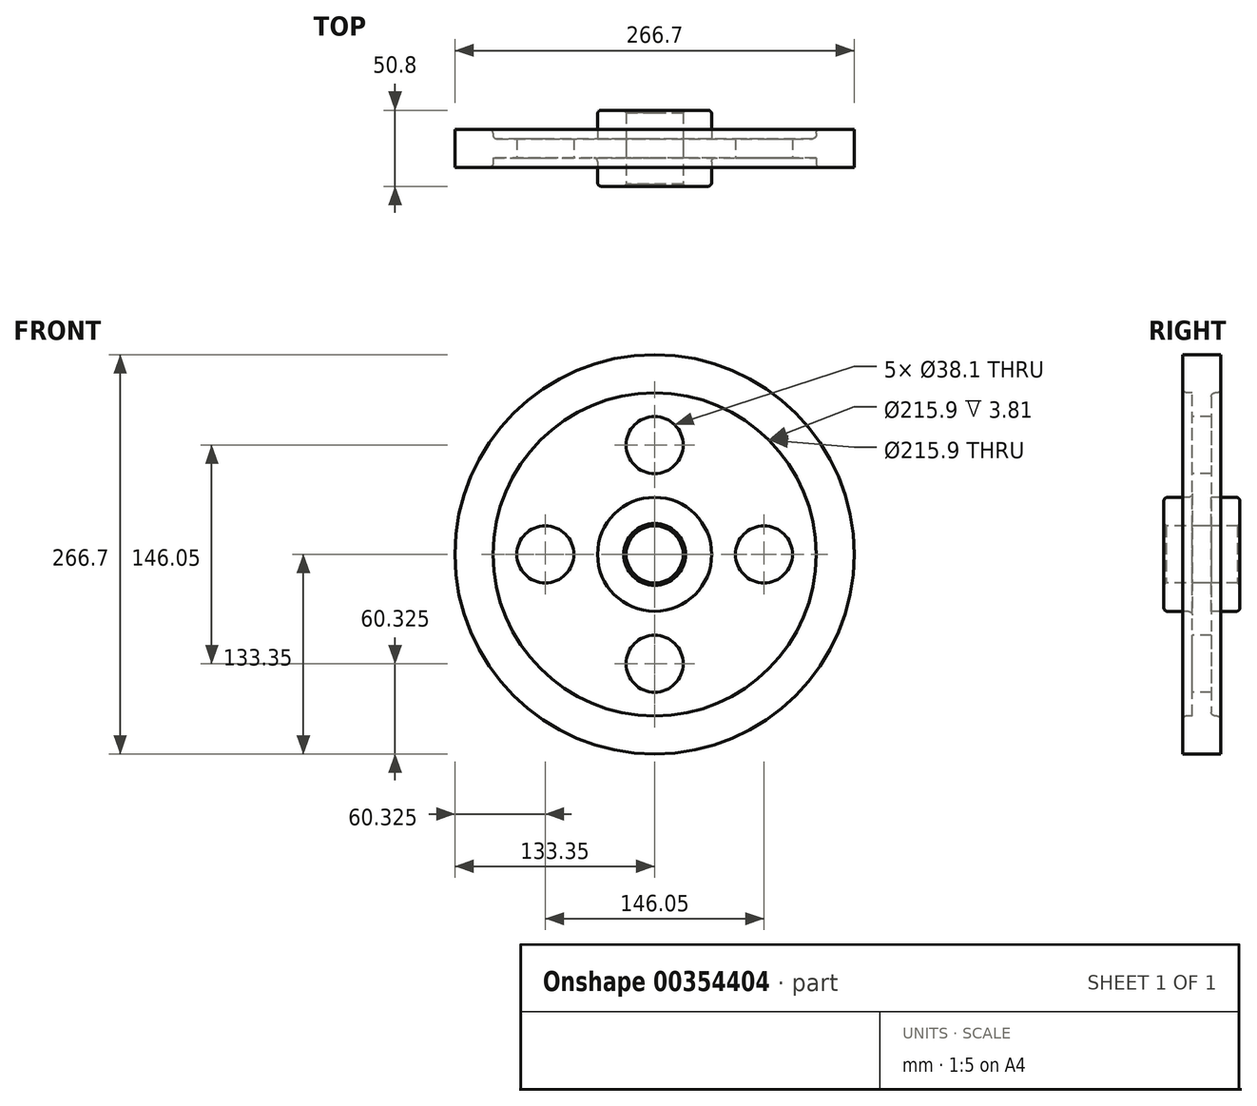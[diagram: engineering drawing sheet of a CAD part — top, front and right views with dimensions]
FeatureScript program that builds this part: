
annotation { "Feature Type Name" : "Feature", "Feature Type Description" : "" }
export const myFeature = defineFeature(function(context is Context, id is Id, definition is map)
    precondition{}
    {
        {
            var Q0;
            Q0=qCreatedBy(makeId("Right.planeOp"),FACE);
            var sketch = newSketch(context, id + "F0", { "sketchPlane" : qUnion([Q0])});
            skLineSegment(sketch, "E0", {"start": v(0, 0) * mm, "end": v(25.4, 0) * mm, "construction": true});
            skLineSegment(sketch, "E1.0", {"start": v(0, 19.05) * mm, "end": v(25.4, 19.05) * mm});
            skLineSegment(sketch, "E2.0", {"start": v(6.35, 38.1) * mm, "end": v(25.4, 38.1) * mm});
            skLineSegment(sketch, "E3.0", {"start": v(6.35, 107.95) * mm, "end": v(12.7, 107.95) * mm});
            skLineSegment(sketch, "E4.0", {"start": v(0, 133.35) * mm, "end": v(12.7, 133.35) * mm});
            skLineSegment(sketch, "E5", {"start": v(0, 107.95) * mm, "end": v(0, 0) * mm, "construction": true});
            skLineSegment(sketch, "E6.0", {"start": v(25.4, 38.1) * mm, "end": v(25.4, 19.05) * mm});
            skLineSegment(sketch, "E7.0", {"start": v(6.35, 107.95) * mm, "end": v(6.35, 38.1) * mm});
            skLineSegment(sketch, "E8.0", {"start": v(12.7, 133.35) * mm, "end": v(12.7, 107.95) * mm});
            skLineSegment(sketch, "E9.MirrorCS", {"start": v(-6.35, 107.95) * mm, "end": v(-6.35, 38.1) * mm});
            skPoint(sketch, "E10.orphan", {"position": v(6.35, 19.05) * mm});
            skPoint(sketch, "E11.orphan", {"position": v(6.35, 133.35) * mm});
            skLineSegment(sketch, "E12.MirrorCS", {"start": v(-12.7, 133.35) * mm, "end": v(-12.7, 107.95) * mm});
            skLineSegment(sketch, "E13.MirrorCS", {"start": v(-6.35, 107.95) * mm, "end": v(-12.7, 107.95) * mm});
            skPoint(sketch, "E14.MirrorP", {"position": v(-6.35, 133.35) * mm});
            skLineSegment(sketch, "E15.MirrorCS", {"start": v(0, 133.35) * mm, "end": v(-12.7, 133.35) * mm});
            skLineSegment(sketch, "E16.MirrorCS", {"start": v(0, 19.05) * mm, "end": v(-25.4, 19.05) * mm});
            skLineSegment(sketch, "E17.MirrorCS", {"start": v(-25.4, 38.1) * mm, "end": v(-25.4, 19.05) * mm});
            skLineSegment(sketch, "E18.MirrorCS", {"start": v(-6.35, 38.1) * mm, "end": v(-25.4, 38.1) * mm});
            skPoint(sketch, "E19.orphan", {"position": v(-6.35, 19.05) * mm});
            skSolve(sketch);
        }
        {
            var Q0;
            Q0=makeQuery(id+"F0.imprint","IMPRINT",FACE,{"disambiguationData":[TD([[makeQuery(id+"F0.imprint","IMPRINT",EDGE,{"derivedFrom":sQuery(id+"F0.wireOp",EDGE,"E1.0")}),1.0]])]});
            var Q1;
            Q1=sQuery(id+"F0.wireOp",EDGE,"E0");
            revolve(context, id + "F1", {"entities" : qUnion([Q0]), "axis" : qUnion([Q1]), "revolveType" : RevolveType.FULL});
        }
        {
            var Q0;
            Q0=makeQuery(id+"F1.opRevolve","SWEPT_FACE",FACE,{"disambiguationData":[OSD([sQuery(id+"F0.wireOp",EDGE,"E9.MirrorCS")])]});
            var sketch = newSketch(context, id + "F2", { "sketchPlane" : qUnion([Q0])});
            skLineSegment(sketch, "E20", {"start": v(0, 0) * mm, "end": v(0, 73.03) * mm});
            skCircle(sketch, "E21", {"center": v(0, 73.03) * mm, "radius": 19.05 * mm});
            skCircle(sketch, "E22.1.0", {"center": v(-73.03, 0) * mm, "radius": 19.05 * mm});
            skCircle(sketch, "E22.2.0", {"center": v(0, -73.03) * mm, "radius": 19.05 * mm});
            skCircle(sketch, "E22.3.0", {"center": v(73.03, 0) * mm, "radius": 19.05 * mm});
            skPoint(sketch, "E22.center", {"position": v(0, 0) * mm});
            skSolve(sketch);
        }
        {
            var Q0;
            Q0=makeQuery(id+"F2.imprint","IMPRINT",FACE,{"disambiguationData":[TD([[makeQuery(id+"F2.imprint","IMPRINT",EDGE,{"derivedFrom":sQuery(id+"F2.wireOp",EDGE,"E21")}),1.0]])]});
            var Q1;
            Q1=makeQuery(id+"F2.imprint","IMPRINT",FACE,{"disambiguationData":[TD([[makeQuery(id+"F2.imprint","IMPRINT",EDGE,{"derivedFrom":sQuery(id+"F2.wireOp",EDGE,"E22.3.0")}),1.0]])]});
            var Q2;
            Q2=makeQuery(id+"F2.imprint","IMPRINT",FACE,{"disambiguationData":[TD([[makeQuery(id+"F2.imprint","IMPRINT",EDGE,{"derivedFrom":sQuery(id+"F2.wireOp",EDGE,"E22.2.0")}),1.0]])]});
            var Q3;
            Q3=makeQuery(id+"F2.imprint","IMPRINT",FACE,{"disambiguationData":[TD([[makeQuery(id+"F2.imprint","IMPRINT",EDGE,{"derivedFrom":sQuery(id+"F2.wireOp",EDGE,"E22.1.0")}),1.0]])]});
            extrude(context, id + "F3", {"entities" : qUnion([Q0, Q1, Q2, Q3]), "operationType" : NewBodyOperationType.REMOVE, "oppositeDirection" : true, "depth" : 25.4 * mm});
        }
        {
            var Q0;
            Q0=makeQuery(id+"F1.opRevolve","SWEPT_EDGE",EDGE,{"disambiguationData":[OSD([sQuery(id+"F0.wireOp",EDGE,"E12.MirrorCS"),sQuery(id+"F0.wireOp",EDGE,"E13.MirrorCS")])]});
            var Q1;
            Q1=makeQuery(id+"F1.opRevolve","SWEPT_EDGE",EDGE,{"disambiguationData":[OSD([sQuery(id+"F0.wireOp",EDGE,"E17.MirrorCS"),sQuery(id+"F0.wireOp",EDGE,"E18.MirrorCS")])]});
            var Q2;
            Q2=makeQuery(id+"F1.opRevolve","SWEPT_EDGE",EDGE,{"disambiguationData":[OSD([sQuery(id+"F0.wireOp",EDGE,"E9.MirrorCS"),sQuery(id+"F0.wireOp",EDGE,"E18.MirrorCS")])]});
            var Q3;
            Q3=makeQuery(id+"F1.opRevolve","SWEPT_EDGE",EDGE,{"disambiguationData":[OSD([sQuery(id+"F0.wireOp",EDGE,"E2.0"),sQuery(id+"F0.wireOp",EDGE,"E6.0")])]});
            fillet(context, id + "F4", {"entities" : qUnion([Q0, Q1, Q2, Q3]), "radius" : 2.54 * mm, "tangentPropagation" : true, "allowEdgeOverflow" : false});
        }
        {
            var Q0;
            {var subQ0=sQuery(id+"F0.wireOp",EDGE,"E6.0");Q0=makeQuery(id+"F4.opFillet","BLEND_EDGE",EDGE,{"blendedFrom":[makeQuery(id+"F1.opRevolve","SWEPT_EDGE",EDGE,{"disambiguationData":[OSD([sQuery(id+"F0.wireOp",EDGE,"E2.0"),subQ0])]}),makeQuery(id+"F1.opRevolve","SWEPT_FACE",FACE,{"disambiguationData":[OSD([subQ0])]})],"blendedInto":[makeQuery(id+"F1.opRevolve","SWEPT_FACE",FACE,{"disambiguationData":[OSD([subQ0])]})]});}
            var Q1;
            {var subQ0=sQuery(id+"F0.wireOp",EDGE,"E2.0");Q1=makeQuery(id+"F4.opFillet","BLEND_EDGE",EDGE,{"blendedFrom":[makeQuery(id+"F1.opRevolve","SWEPT_EDGE",EDGE,{"disambiguationData":[OSD([subQ0,sQuery(id+"F0.wireOp",EDGE,"E6.0")])]}),makeQuery(id+"F1.opRevolve","SWEPT_FACE",FACE,{"disambiguationData":[OSD([subQ0])]})],"blendedInto":[makeQuery(id+"F1.opRevolve","SWEPT_FACE",FACE,{"disambiguationData":[OSD([subQ0])]})]});}
            var Q2;
            Q2=makeQuery(id+"F1.opRevolve","SWEPT_EDGE",EDGE,{"disambiguationData":[OSD([sQuery(id+"F0.wireOp",EDGE,"E3.0"),sQuery(id+"F0.wireOp",EDGE,"E7.0")])]});
            var Q3;
            Q3=makeQuery(id+"F1.opRevolve","SWEPT_EDGE",EDGE,{"disambiguationData":[OSD([sQuery(id+"F0.wireOp",EDGE,"E3.0"),sQuery(id+"F0.wireOp",EDGE,"E8.0")])]});
            fillet(context, id + "F5", {"entities" : qUnion([Q0, Q1, Q2, Q3]), "radius" : 2.54 * mm, "tangentPropagation" : true, "allowEdgeOverflow" : false});
        }
        {
            var Q0;
            Q0=makeQuery(id+"F1.opRevolve","SWEPT_EDGE",EDGE,{"disambiguationData":[OSD([sQuery(id+"F0.wireOp",EDGE,"E16.MirrorCS"),sQuery(id+"F0.wireOp",EDGE,"E17.MirrorCS")])]});
            var Q1;
            Q1=makeQuery(id+"F1.opRevolve","SWEPT_FACE",FACE,{"disambiguationData":[OSD([sQuery(id+"F0.wireOp",EDGE,"E1.0"),sQuery(id+"F0.wireOp",EDGE,"E16.MirrorCS")])]});
            chamfer(context, id + "F6", {"entities" : qUnion([Q0, Q1]), "width" : 1.59 * mm, "tangentPropagation" : true});
        }
    });
